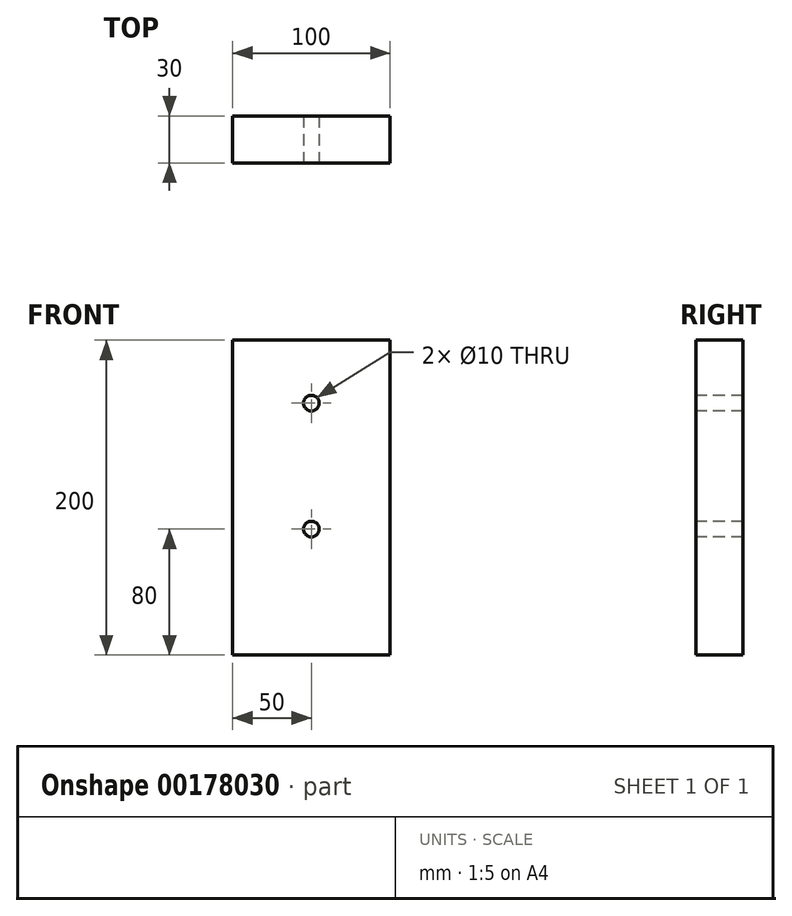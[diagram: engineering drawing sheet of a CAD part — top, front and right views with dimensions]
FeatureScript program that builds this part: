
annotation { "Feature Type Name" : "Feature", "Feature Type Description" : "" }
export const myFeature = defineFeature(function(context is Context, id is Id, definition is map)
    precondition{}
    {
        {
            var Q0;
            Q0=qCreatedBy(makeId("Front.planeOp"),FACE);
            var sketch = newSketch(context, id + "F0", { "sketchPlane" : qUnion([Q0])});
            skLineSegment(sketch, "E0", {"start": v(-50, 0) * mm, "end": v(-50, 100) * mm});
            skLineSegment(sketch, "E1", {"start": v(-50, 100) * mm, "end": v(0, 100) * mm});
            skLineSegment(sketch, "E2", {"start": v(0, 100) * mm, "end": v(50, 100) * mm});
            skLineSegment(sketch, "E3", {"start": v(50, 100) * mm, "end": v(50, 0) * mm});
            skLineSegment(sketch, "E4", {"start": v(-50, 0) * mm, "end": v(50, 0) * mm, "construction": true});
            skLineSegment(sketch, "E5.MirrorCS", {"start": v(-50, 0) * mm, "end": v(-50, -100) * mm});
            skLineSegment(sketch, "E6.MirrorCS", {"start": v(50, -100) * mm, "end": v(50, 0) * mm});
            skLineSegment(sketch, "E7.MirrorCS", {"start": v(0, -100) * mm, "end": v(50, -100) * mm});
            skLineSegment(sketch, "E8.MirrorCS", {"start": v(-50, -100) * mm, "end": v(0, -100) * mm});
            skSolve(sketch);
        }
        {
            var Q0;
            Q0=makeQuery(id+"F0.imprint","IMPRINT",FACE,{"disambiguationData":[TD([[makeQuery(id+"F0.imprint","IMPRINT",EDGE,{"derivedFrom":sQuery(id+"F0.wireOp",EDGE,"E0")}),-1.0]])]});
            extrude(context, id + "F1", {"entities" : qUnion([Q0]), "depth" : 30 * mm});
        }
        {
            var Q0;
            Q0=makeQuery(id+"F1.opExtrude","CAP_FACE",FACE,{"disambiguationData":[OSD([sQuery(id+"F0.wireOp",EDGE,"E0"),sQuery(id+"F0.wireOp",EDGE,"E1"),sQuery(id+"F0.wireOp",EDGE,"E2"),sQuery(id+"F0.wireOp",EDGE,"E3"),sQuery(id+"F0.wireOp",EDGE,"E5.MirrorCS"),sQuery(id+"F0.wireOp",EDGE,"E6.MirrorCS"),sQuery(id+"F0.wireOp",EDGE,"E7.MirrorCS"),sQuery(id+"F0.wireOp",EDGE,"E8.MirrorCS")])],"isStart":false});
            var sketch = newSketch(context, id + "F2", { "sketchPlane" : qUnion([Q0])});
            skCircle(sketch, "E9", {"center": v(0, -20) * mm, "radius": 5 * mm});
            skCircle(sketch, "E10", {"center": v(0, 60) * mm, "radius": 5 * mm});
            skSolve(sketch);
        }
        {
            var Q0;
            Q0=makeQuery(id+"F2.imprint","IMPRINT",FACE,{"disambiguationData":[TD([[makeQuery(id+"F2.imprint","IMPRINT",EDGE,{"derivedFrom":sQuery(id+"F2.wireOp",EDGE,"E10")}),1.0]])]});
            extrude(context, id + "F3", {"entities" : qUnion([Q0]), "operationType" : NewBodyOperationType.REMOVE, "oppositeDirection" : true, "depth" : 30 * mm});
        }
        {
            var Q0;
            Q0 = qSketchRegion(id + "F2", true);
            extrude(context, id + "F4", {"entities" : qUnion([Q0]), "operationType" : NewBodyOperationType.REMOVE, "oppositeDirection" : true, "depth" : 30 * mm});
        }
    });
